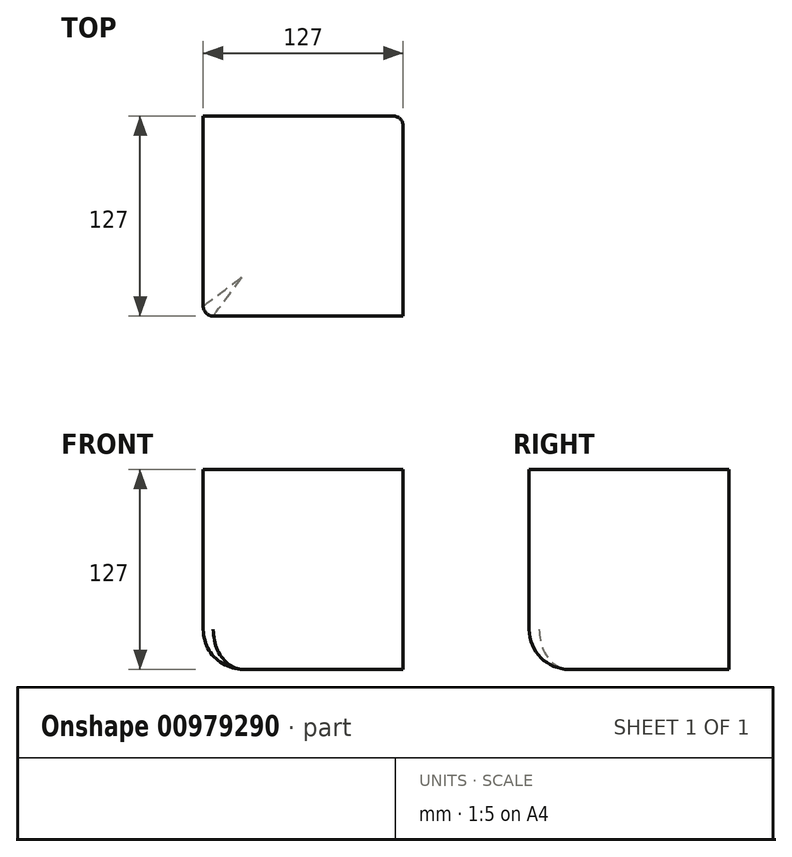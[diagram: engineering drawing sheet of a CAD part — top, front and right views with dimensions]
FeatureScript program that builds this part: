
annotation { "Feature Type Name" : "Feature", "Feature Type Description" : "" }
export const myFeature = defineFeature(function(context is Context, id is Id, definition is map)
    precondition{}
    {
        {
            var Q0;
            Q0=qCreatedBy(makeId("Top.planeOp"),FACE);
            var sketch = newSketch(context, id + "F0", { "sketchPlane" : qUnion([Q0])});
            skLineSegment(sketch, "E0.bottom", {"start": v(63.5, -63.5) * mm, "end": v(-57.15, -63.5) * mm});
            skLineSegment(sketch, "E0.top", {"start": v(57.15, 63.5) * mm, "end": v(-63.5, 63.5) * mm});
            skLineSegment(sketch, "E0.left", {"start": v(63.5, -63.5) * mm, "end": v(63.5, 57.15) * mm});
            skLineSegment(sketch, "E0.right", {"start": v(-63.5, -57.15) * mm, "end": v(-63.5, 63.5) * mm});
            skPoint(sketch, "E0.middle", {"position": v(0, 0) * mm});
            skPoint(sketch, "E1.visualSharp", {"position": v(63.5, 63.5) * mm});
            skArc(sketch, "E1.filletArc", {"start": v(63.5, 57.15) * mm, "mid": v(61.64, 61.64) * mm, "end": v(57.15, 63.5) * mm});
            skPoint(sketch, "E2.visualSharp", {"position": v(-63.5, -63.5) * mm});
            skArc(sketch, "E2.filletArc", {"start": v(-63.5, -57.15) * mm, "mid": v(-61.64, -61.64) * mm, "end": v(-57.15, -63.5) * mm});
            skSolve(sketch);
        }
        {
            var Q0;
            Q0=makeQuery(id+"F0.imprint","IMPRINT",FACE,{"disambiguationData":[TD([[makeQuery(id+"F0.imprint","IMPRINT",EDGE,{"derivedFrom":sQuery(id+"F0.wireOp",EDGE,"E0.bottom")}),-1.0]])]});
            extrude(context, id + "F1", {"entities" : qUnion([Q0]), "oppositeDirection" : true, "depth" : 127 * mm, "offsetDistance" : 25.4 * mm});
        }
        {
            var Q0;
            Q0=makeQuery(id+"F1.opExtrude","CAP_EDGE",EDGE,{"disambiguationData":[OSD([sQuery(id+"F0.wireOp",EDGE,"E0.right")])],"isStart":false});
            fillet(context, id + "F2", {"entities" : qUnion([Q0]), "radius" : 25.4 * mm, "tangentPropagation" : true, "allowEdgeOverflow" : false});
        }
    });
